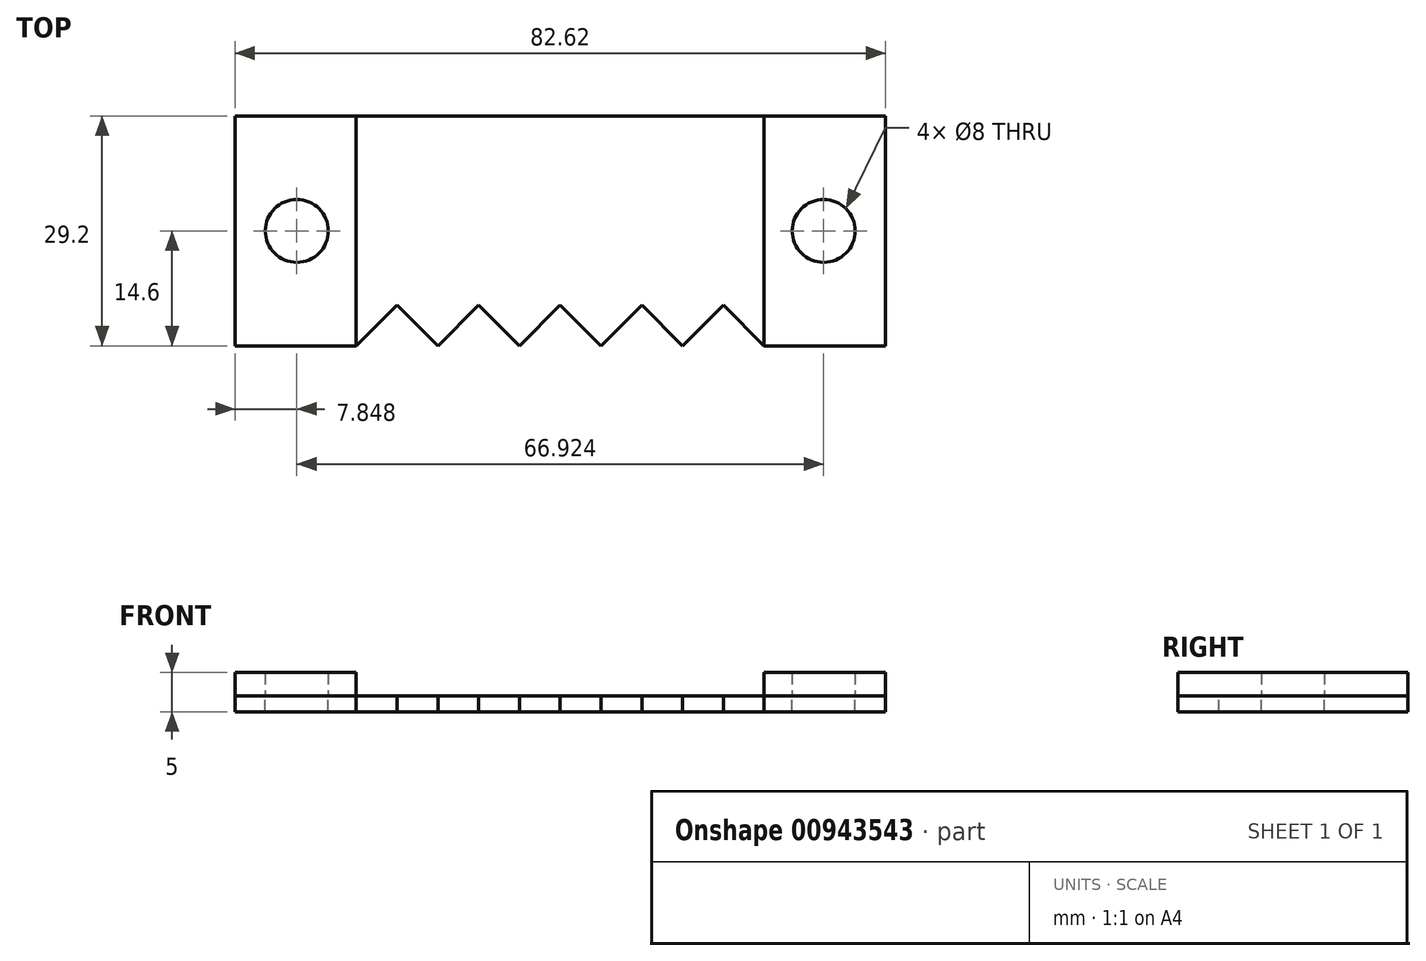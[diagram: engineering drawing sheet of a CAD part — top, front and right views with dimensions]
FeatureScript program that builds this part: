
annotation { "Feature Type Name" : "Feature", "Feature Type Description" : "" }
export const myFeature = defineFeature(function(context is Context, id is Id, definition is map)
    precondition{}
    {
        {
            var Q0;
            Q0=qCreatedBy(makeId("Top.planeOp"),FACE);
            var sketch = newSketch(context, id + "F0", { "sketchPlane" : qUnion([Q0])});
            skLineSegment(sketch, "E0.bottom", {"start": v(-41.3, 14.6) * mm, "end": v(-25.9, 14.6) * mm});
            skLineSegment(sketch, "E0.top", {"start": v(-41.3, -14.6) * mm, "end": v(-25.9, -14.6) * mm});
            skLineSegment(sketch, "E0.left", {"start": v(-41.3, 14.6) * mm, "end": v(-41.3, -14.6) * mm});
            skLineSegment(sketch, "E0.right", {"start": v(-25.9, 14.6) * mm, "end": v(-25.9, -14.6) * mm});
            skLineSegment(sketch, "E1.bottom", {"start": v(25.9, 14.6) * mm, "end": v(41.3, 14.6) * mm});
            skLineSegment(sketch, "E1.top", {"start": v(25.9, -14.6) * mm, "end": v(41.3, -14.6) * mm});
            skLineSegment(sketch, "E1.left", {"start": v(25.9, 14.6) * mm, "end": v(25.9, -14.6) * mm});
            skLineSegment(sketch, "E1.right", {"start": v(41.3, 14.6) * mm, "end": v(41.3, -14.6) * mm});
            skLineSegment(sketch, "E2", {"start": v(-25.9, 14.6) * mm, "end": v(25.9, 14.6) * mm});
            skLineSegment(sketch, "E3", {"start": v(-25.9, -14.6) * mm, "end": v(-20.72, -9.42) * mm});
            skLineSegment(sketch, "E4", {"start": v(-20.72, -9.42) * mm, "end": v(-15.54, -14.6) * mm});
            skLineSegment(sketch, "E5.1.0.0", {"start": v(-15.54, -14.6) * mm, "end": v(-10.36, -9.42) * mm});
            skLineSegment(sketch, "E5.1.0.1", {"start": v(-10.36, -9.42) * mm, "end": v(-5.18, -14.6) * mm});
            skLineSegment(sketch, "E5.2.0.0", {"start": v(-5.18, -14.6) * mm, "end": v(0, -9.42) * mm});
            skLineSegment(sketch, "E5.2.0.1", {"start": v(0, -9.42) * mm, "end": v(5.18, -14.6) * mm});
            skLineSegment(sketch, "E5.3.0.0", {"start": v(5.18, -14.6) * mm, "end": v(10.36, -9.42) * mm});
            skLineSegment(sketch, "E5.3.0.1", {"start": v(10.36, -9.42) * mm, "end": v(15.54, -14.6) * mm});
            skLineSegment(sketch, "E5.4.0.0", {"start": v(15.54, -14.6) * mm, "end": v(20.72, -9.42) * mm});
            skLineSegment(sketch, "E5.4.0.1", {"start": v(20.72, -9.42) * mm, "end": v(25.9, -14.6) * mm});
            skLineSegment(sketch, "E5.direction1", {"start": v(-25.9, -14.6) * mm, "end": v(-15.54, -14.6) * mm, "construction": true});
            skCircle(sketch, "E6", {"center": v(-33.46, 0) * mm, "radius": 4 * mm});
            skCircle(sketch, "E7", {"center": v(33.46, 0) * mm, "radius": 4 * mm});
            skSolve(sketch);
        }
        {
            var Q0;
            Q0=makeQuery(id+"F0.imprint","IMPRINT",FACE,{"disambiguationData":[TD([[makeQuery(id+"F0.imprint","IMPRINT",EDGE,{"derivedFrom":sQuery(id+"F0.wireOp",EDGE,"E0.bottom")}),-1.0]])]});
            var Q1;
            Q1=makeQuery(id+"F0.imprint","IMPRINT",FACE,{"disambiguationData":[TD([[makeQuery(id+"F0.imprint","IMPRINT",EDGE,{"derivedFrom":sQuery(id+"F0.wireOp",EDGE,"E1.bottom")}),-1.0]])]});
            extrude(context, id + "F1", {"entities" : qUnion([Q0, Q1]), "depth" : 3 * mm, "offsetDistance" : 25 * mm});
        }
        {
            var Q0;
            Q0=makeQuery(id+"F0.imprint","IMPRINT",FACE,{"disambiguationData":[TD([[makeQuery(id+"F0.imprint","IMPRINT",EDGE,{"derivedFrom":sQuery(id+"F0.wireOp",EDGE,"E0.bottom")}),-1.0]])]});
            var Q1;
            Q1=makeQuery(id+"F0.imprint","IMPRINT",FACE,{"disambiguationData":[TD([[makeQuery(id+"F0.imprint","IMPRINT",EDGE,{"derivedFrom":sQuery(id+"F0.wireOp",EDGE,"E0.right")}),1.0]])]});
            var Q2;
            Q2=makeQuery(id+"F0.imprint","IMPRINT",FACE,{"disambiguationData":[TD([[makeQuery(id+"F0.imprint","IMPRINT",EDGE,{"derivedFrom":sQuery(id+"F0.wireOp",EDGE,"E1.bottom")}),-1.0]])]});
            extrude(context, id + "F2", {"entities" : qUnion([Q0, Q1, Q2]), "oppositeDirection" : true, "depth" : 2 * mm, "offsetDistance" : 25 * mm});
        }
    });
